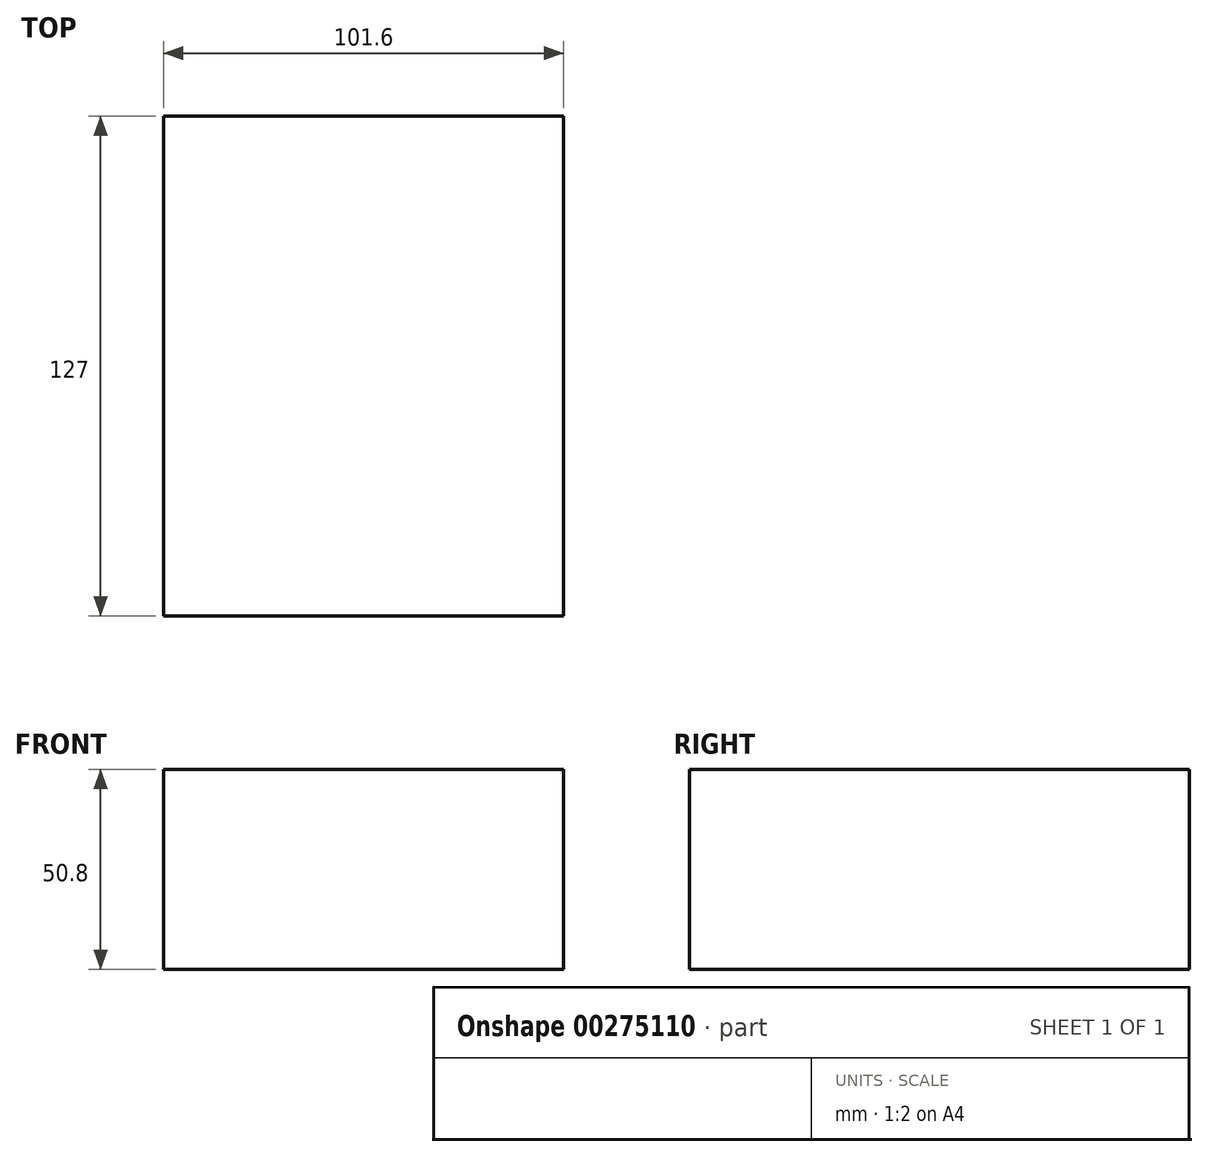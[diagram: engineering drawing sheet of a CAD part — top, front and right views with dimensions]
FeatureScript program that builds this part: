
annotation { "Feature Type Name" : "Feature", "Feature Type Description" : "" }
export const myFeature = defineFeature(function(context is Context, id is Id, definition is map)
    precondition{}
    {
        {
            var Q0;
            Q0=qCreatedBy(makeId("Front.planeOp"),FACE);
            var sketch = newSketch(context, id + "F0", { "sketchPlane" : qUnion([Q0])});
            skLineSegment(sketch, "E0.bottom", {"start": v(50.8, 25.4) * mm, "end": v(-50.8, 25.4) * mm});
            skLineSegment(sketch, "E0.top", {"start": v(50.8, -25.4) * mm, "end": v(-50.8, -25.4) * mm});
            skLineSegment(sketch, "E0.left", {"start": v(50.8, 25.4) * mm, "end": v(50.8, -25.4) * mm});
            skLineSegment(sketch, "E0.right", {"start": v(-50.8, 25.4) * mm, "end": v(-50.8, -25.4) * mm});
            skPoint(sketch, "E0.middle", {"position": v(0, 0) * mm});
            skSolve(sketch);
        }
        {
            var Q0;
            Q0=makeQuery(id+"F0.imprint","IMPRINT",FACE,{"disambiguationData":[TD([[makeQuery(id+"F0.imprint","IMPRINT",EDGE,{"derivedFrom":sQuery(id+"F0.wireOp",EDGE,"E0.bottom")}),1.0]])]});
            extrude(context, id + "F1", {"entities" : qUnion([Q0]), "depth" : 127 * mm});
        }
    });
